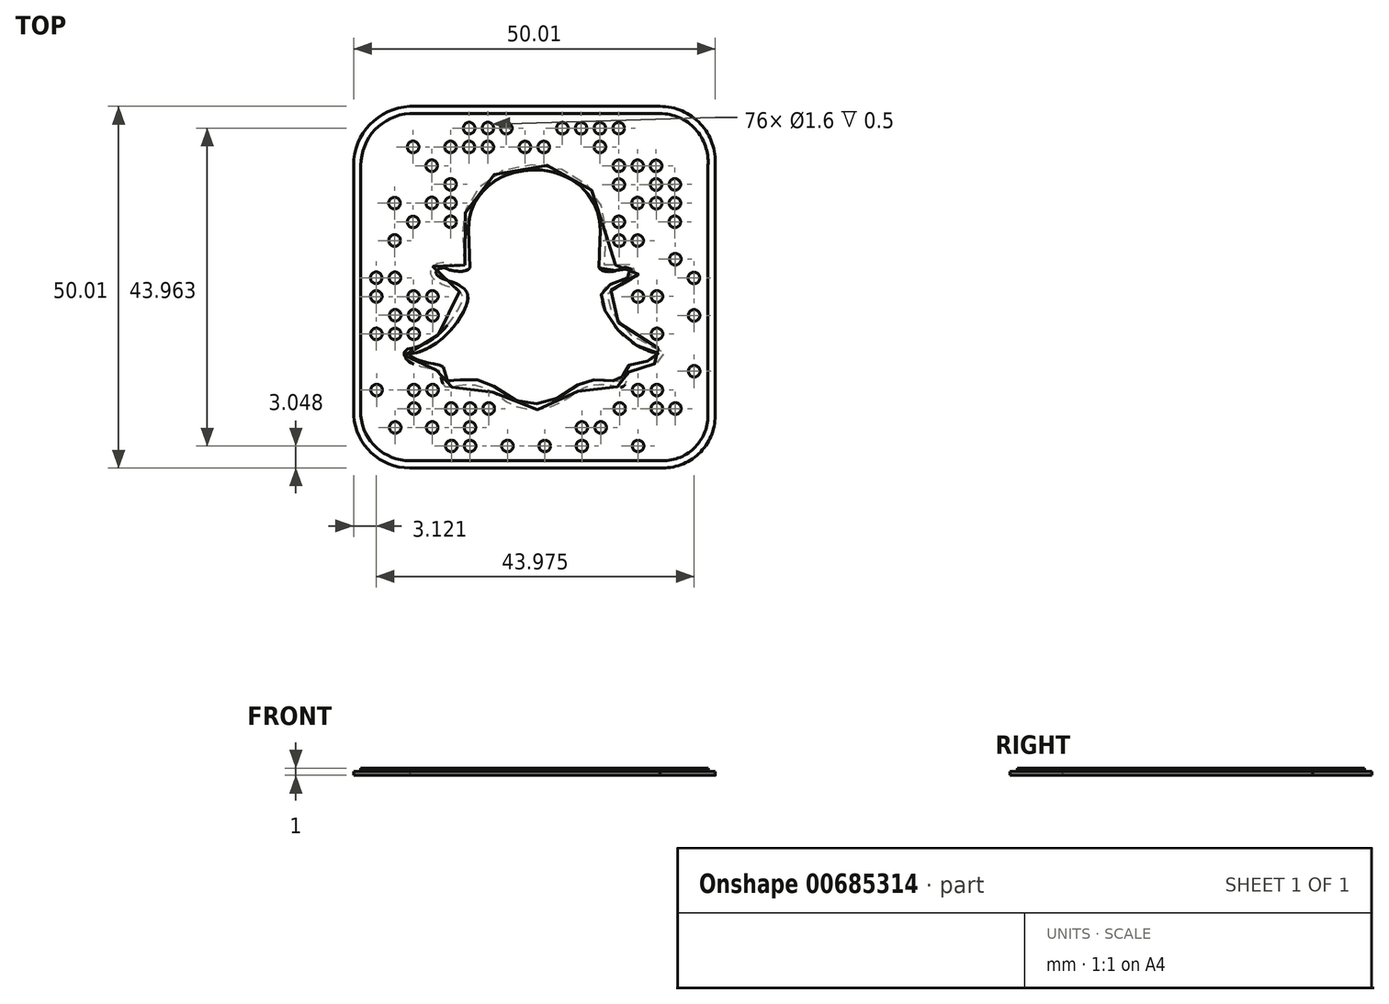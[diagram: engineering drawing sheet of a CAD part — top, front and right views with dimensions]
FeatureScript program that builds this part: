
annotation { "Feature Type Name" : "Feature", "Feature Type Description" : "" }
export const myFeature = defineFeature(function(context is Context, id is Id, definition is map)
    precondition{}
    {
        {
            var Q0;
            Q0=qCreatedBy(makeId("Top.planeOp"),FACE);
            var sketch = newSketch(context, id + "F0", { "sketchPlane" : qUnion([Q0])});
            skLineSegment(sketch, "E0", {"start": v(-18.15, 26.17) * mm, "end": v(16.46, 26.17) * mm});
            skLineSegment(sketch, "E1", {"start": v(-18.15, -23.83) * mm, "end": v(16.46, -23.83) * mm});
            skLineSegment(sketch, "E2", {"start": v(24.09, -16.6) * mm, "end": v(24.09, 18) * mm});
            skLineSegment(sketch, "E3", {"start": v(-25.91, -16.6) * mm, "end": v(-25.91, 18) * mm});
            skArc(sketch, "E4", {"start": v(-25.91, 18) * mm, "mid": v(-23.66, 23.64) * mm, "end": v(-18.15, 26.17) * mm});
            skArc(sketch, "E5", {"start": v(16.46, 26.17) * mm, "mid": v(22.05, 23.75) * mm, "end": v(24.09, 18) * mm});
            skArc(sketch, "E6", {"start": v(24.09, -16.6) * mm, "mid": v(21.83, -21.85) * mm, "end": v(16.46, -23.83) * mm});
            skArc(sketch, "E7", {"start": v(-18.15, -23.83) * mm, "mid": v(-23.45, -21.74) * mm, "end": v(-25.91, -16.6) * mm});
            skSolve(sketch);
        }
        {
            var Q0;
            Q0 = qSketchRegion(id + "F0", true);
            var Q1;
            Q1=makeQuery(id+"F0.imprint","IMPRINT",FACE,{"disambiguationData":[TD([[makeQuery(id+"F0.imprint","IMPRINT",EDGE,{"derivedFrom":sQuery(id+"F0.wireOp",EDGE,"E0")}),-1.0]])]});
            extrude(context, id + "F1", {"entities" : qUnion([Q0, Q1]), "depth" : 0.5 * mm, "offsetDistance" : 25 * mm});
        }
        {
            var Q0;
            Q0=makeQuery(id+"F1.opExtrude","CAP_FACE",FACE,{"disambiguationData":[OSD([sQuery(id+"F0.wireOp",EDGE,"E0"),sQuery(id+"F0.wireOp",EDGE,"E1"),sQuery(id+"F0.wireOp",EDGE,"E2"),sQuery(id+"F0.wireOp",EDGE,"E3"),sQuery(id+"F0.wireOp",EDGE,"E4"),sQuery(id+"F0.wireOp",EDGE,"E5"),sQuery(id+"F0.wireOp",EDGE,"E6"),sQuery(id+"F0.wireOp",EDGE,"E7")])],"isStart":false});
            var sketch = newSketch(context, id + "F2", { "sketchPlane" : qUnion([Q0])});
            skLineSegment(sketch, "E8", {"start": v(-18.15, 25.17) * mm, "end": v(16.46, 25.17) * mm});
            skLineSegment(sketch, "E9", {"start": v(23.09, 18) * mm, "end": v(23.09, -16.6) * mm});
            skLineSegment(sketch, "E10", {"start": v(16.46, -22.83) * mm, "end": v(-18.15, -22.83) * mm});
            skLineSegment(sketch, "E11", {"start": v(-24.91, -16.6) * mm, "end": v(-24.91, 18) * mm});
            skArc(sketch, "E12", {"start": v(-24.91, 18) * mm, "mid": v(-22.96, 22.94) * mm, "end": v(-18.15, 25.17) * mm});
            skArc(sketch, "E13", {"start": v(16.46, 25.17) * mm, "mid": v(21.34, 23.04) * mm, "end": v(23.09, 18) * mm});
            skArc(sketch, "E14", {"start": v(23.09, -16.6) * mm, "mid": v(21.12, -21.15) * mm, "end": v(16.46, -22.83) * mm});
            skArc(sketch, "E15", {"start": v(-18.15, -22.83) * mm, "mid": v(-22.74, -21.03) * mm, "end": v(-24.91, -16.6) * mm});
            skSolve(sketch);
        }
        {
            var Q0;
            Q0 = qSketchRegion(id + "F2", true);
            extrude(context, id + "F3", {"entities" : qUnion([Q0]), "operationType" : NewBodyOperationType.ADD, "depth" : 0.5 * mm, "offsetDistance" : 25 * mm});
        }
        {
            var Q0;
            Q0=makeQuery(id+"F1.opExtrude","CAP_FACE",FACE,{"disambiguationData":[OSD([sQuery(id+"F0.wireOp",EDGE,"E0"),sQuery(id+"F0.wireOp",EDGE,"E1"),sQuery(id+"F0.wireOp",EDGE,"E2"),sQuery(id+"F0.wireOp",EDGE,"E3"),sQuery(id+"F0.wireOp",EDGE,"E4"),sQuery(id+"F0.wireOp",EDGE,"E5"),sQuery(id+"F0.wireOp",EDGE,"E6"),sQuery(id+"F0.wireOp",EDGE,"E7")])],"isStart":false});
            var sketch = newSketch(context, id + "F4", { "sketchPlane" : qUnion([Q0])});
            skCircle(sketch, "E16", {"center": v(-2.22, 20.55) * mm, "radius": 0.8 * mm});
            skPoint(sketch, "E16.first.point", {"position": v(-2.2, 21.35) * mm});
            skPoint(sketch, "E16.second.point", {"position": v(-2.2, 19.75) * mm});
            skPoint(sketch, "E16.third.point", {"position": v(-1.7, 19.95) * mm});
            skCircle(sketch, "E17", {"center": v(0.39, 20.55) * mm, "radius": 0.8 * mm});
            skCircle(sketch, "E18", {"center": v(2.95, 23.15) * mm, "radius": 0.8 * mm});
            skCircle(sketch, "E19", {"center": v(5.55, 23.14) * mm, "radius": 0.8 * mm});
            skCircle(sketch, "E20", {"center": v(8.14, 23.15) * mm, "radius": 0.8 * mm});
            skCircle(sketch, "E21", {"center": v(10.75, 23.16) * mm, "radius": 0.8 * mm});
            skCircle(sketch, "E22", {"center": v(-4.79, 23.16) * mm, "radius": 0.8 * mm});
            skCircle(sketch, "E23", {"center": v(-7.34, 23.17) * mm, "radius": 0.8 * mm});
            skCircle(sketch, "E24", {"center": v(-9.94, 23.16) * mm, "radius": 0.8 * mm});
            skCircle(sketch, "E25", {"center": v(8.15, 20.58) * mm, "radius": 0.8 * mm});
            skCircle(sketch, "E26", {"center": v(-7.35, 20.58) * mm, "radius": 0.8 * mm});
            skCircle(sketch, "E27", {"center": v(-9.95, 20.56) * mm, "radius": 0.8 * mm});
            skCircle(sketch, "E28", {"center": v(-12.52, 20.57) * mm, "radius": 0.8 * mm});
            skCircle(sketch, "E29", {"center": v(-17.69, 20.57) * mm, "radius": 0.8 * mm});
            skCircle(sketch, "E30", {"center": v(-15.1, 17.97) * mm, "radius": 0.8 * mm});
            skCircle(sketch, "E31", {"center": v(10.78, 17.95) * mm, "radius": 0.8 * mm});
            skCircle(sketch, "E32", {"center": v(13.37, 17.95) * mm, "radius": 0.8 * mm});
            skCircle(sketch, "E33", {"center": v(15.92, 17.95) * mm, "radius": 0.8 * mm});
            skCircle(sketch, "E34", {"center": v(-12.5, 15.39) * mm, "radius": 0.8 * mm});
            skCircle(sketch, "E35", {"center": v(10.77, 15.36) * mm, "radius": 0.8 * mm});
            skCircle(sketch, "E36", {"center": v(15.91, 15.37) * mm, "radius": 0.8 * mm});
            skCircle(sketch, "E37", {"center": v(18.52, 15.38) * mm, "radius": 0.8 * mm});
            skCircle(sketch, "E38", {"center": v(18.52, 12.8) * mm, "radius": 0.8 * mm});
            skCircle(sketch, "E39", {"center": v(15.93, 12.79) * mm, "radius": 0.8 * mm});
            skCircle(sketch, "E40", {"center": v(13.34, 12.8) * mm, "radius": 0.8 * mm});
            skCircle(sketch, "E41", {"center": v(-12.52, 12.82) * mm, "radius": 0.8 * mm});
            skCircle(sketch, "E42", {"center": v(-15.1, 12.82) * mm, "radius": 0.8 * mm});
            skCircle(sketch, "E43", {"center": v(-20.26, 12.8) * mm, "radius": 0.8 * mm});
            skCircle(sketch, "E44", {"center": v(18.5, 10.22) * mm, "radius": 0.8 * mm});
            skCircle(sketch, "E45", {"center": v(10.77, 10.2) * mm, "radius": 0.8 * mm});
            skCircle(sketch, "E46", {"center": v(-12.5, 10.21) * mm, "radius": 0.8 * mm});
            skCircle(sketch, "E47", {"center": v(-17.68, 10.2) * mm, "radius": 0.8 * mm});
            skCircle(sketch, "E48", {"center": v(-20.24, 7.63) * mm, "radius": 0.8 * mm});
            skCircle(sketch, "E49", {"center": v(13.37, 7.62) * mm, "radius": 0.8 * mm});
            skCircle(sketch, "E50", {"center": v(10.81, 7.6) * mm, "radius": 0.8 * mm});
            skCircle(sketch, "E51", {"center": v(18.57, 5.04) * mm, "radius": 0.8 * mm});
            skCircle(sketch, "E52", {"center": v(-20.2, 2.46) * mm, "radius": 0.8 * mm});
            skCircle(sketch, "E53", {"center": v(-22.79, 2.47) * mm, "radius": 0.8 * mm});
            skCircle(sketch, "E54", {"center": v(21.15, 2.45) * mm, "radius": 0.8 * mm});
            skCircle(sketch, "E55", {"center": v(16.03, -0.12) * mm, "radius": 0.8 * mm});
            skCircle(sketch, "E56", {"center": v(13.42, -0.14) * mm, "radius": 0.8 * mm});
            skCircle(sketch, "E57", {"center": v(-15.02, -0.12) * mm, "radius": 0.8 * mm});
            skCircle(sketch, "E58", {"center": v(-17.6, -0.12) * mm, "radius": 0.8 * mm});
            skCircle(sketch, "E59", {"center": v(-22.78, -0.12) * mm, "radius": 0.8 * mm});
            skCircle(sketch, "E60", {"center": v(-20.16, -2.72) * mm, "radius": 0.8 * mm});
            skCircle(sketch, "E61", {"center": v(-17.56, -2.72) * mm, "radius": 0.8 * mm});
            skCircle(sketch, "E62", {"center": v(-14.98, -2.73) * mm, "radius": 0.8 * mm});
            skCircle(sketch, "E63", {"center": v(21.17, -2.73) * mm, "radius": 0.8 * mm});
            skCircle(sketch, "E64", {"center": v(16.04, -5.3) * mm, "radius": 0.8 * mm});
            skCircle(sketch, "E65", {"center": v(-17.58, -5.3) * mm, "radius": 0.8 * mm});
            skCircle(sketch, "E66", {"center": v(-20.17, -5.3) * mm, "radius": 0.8 * mm});
            skCircle(sketch, "E67", {"center": v(-22.75, -5.3) * mm, "radius": 0.8 * mm});
            skCircle(sketch, "E68", {"center": v(21.19, -10.46) * mm, "radius": 0.8 * mm});
            skCircle(sketch, "E69", {"center": v(16.02, -13.06) * mm, "radius": 0.8 * mm});
            skCircle(sketch, "E70", {"center": v(13.41, -13.06) * mm, "radius": 0.8 * mm});
            skCircle(sketch, "E71", {"center": v(-15, -13.06) * mm, "radius": 0.8 * mm});
            skCircle(sketch, "E72", {"center": v(-17.57, -13.06) * mm, "radius": 0.8 * mm});
            skCircle(sketch, "E73", {"center": v(-22.73, -13.06) * mm, "radius": 0.8 * mm});
            skCircle(sketch, "E74", {"center": v(-17.56, -15.61) * mm, "radius": 0.8 * mm});
            skCircle(sketch, "E75", {"center": v(-12.42, -15.61) * mm, "radius": 0.8 * mm});
            skCircle(sketch, "E76", {"center": v(-9.8, -15.61) * mm, "radius": 0.8 * mm});
            skCircle(sketch, "E77", {"center": v(-7.23, -15.61) * mm, "radius": 0.8 * mm});
            skCircle(sketch, "E78", {"center": v(10.87, -15.61) * mm, "radius": 0.8 * mm});
            skCircle(sketch, "E79", {"center": v(16.02, -15.61) * mm, "radius": 0.8 * mm});
            skCircle(sketch, "E80", {"center": v(18.59, -15.61) * mm, "radius": 0.8 * mm});
            skCircle(sketch, "E81", {"center": v(8.26, -18.23) * mm, "radius": 0.8 * mm});
            skCircle(sketch, "E82", {"center": v(5.65, -18.23) * mm, "radius": 0.8 * mm});
            skCircle(sketch, "E83", {"center": v(-9.82, -18.23) * mm, "radius": 0.8 * mm});
            skCircle(sketch, "E84", {"center": v(-15.04, -18.23) * mm, "radius": 0.8 * mm});
            skCircle(sketch, "E85", {"center": v(-20.16, -18.23) * mm, "radius": 0.8 * mm});
            skCircle(sketch, "E86", {"center": v(-12.4, -20.8) * mm, "radius": 0.8 * mm});
            skCircle(sketch, "E87", {"center": v(-9.82, -20.8) * mm, "radius": 0.8 * mm});
            skCircle(sketch, "E88", {"center": v(-4.65, -20.8) * mm, "radius": 0.8 * mm});
            skCircle(sketch, "E89", {"center": v(0.52, -20.8) * mm, "radius": 0.8 * mm});
            skCircle(sketch, "E90", {"center": v(5.66, -20.8) * mm, "radius": 0.8 * mm});
            skCircle(sketch, "E91", {"center": v(13.42, -20.8) * mm, "radius": 0.8 * mm});
            skSolve(sketch);
        }
        {
            var Q0;
            Q0 = qSketchRegion(id + "F4", true);
            extrude(context, id + "F5", {"entities" : qUnion([Q0]), "operationType" : NewBodyOperationType.REMOVE, "depth" : 0.5 * mm, "offsetDistance" : 25 * mm});
        }
        {
            var Q0;
            Q0=makeQuery(id+"F1.opExtrude","CAP_FACE",FACE,{"disambiguationData":[OSD([sQuery(id+"F0.wireOp",EDGE,"E0"),sQuery(id+"F0.wireOp",EDGE,"E1"),sQuery(id+"F0.wireOp",EDGE,"E2"),sQuery(id+"F0.wireOp",EDGE,"E3"),sQuery(id+"F0.wireOp",EDGE,"E4"),sQuery(id+"F0.wireOp",EDGE,"E5"),sQuery(id+"F0.wireOp",EDGE,"E6"),sQuery(id+"F0.wireOp",EDGE,"E7")])],"isStart":false});
            var sketch = newSketch(context, id + "F6", { "sketchPlane" : qUnion([Q0])});
            skLineSegment(sketch, "E92", {"start": v(-9.83, 3.85) * mm, "end": v(-10.03, 9.17) * mm});
            skFitSpline(sketch, "E93", {"points": [v(-10.03, 9.17) * mm, v(-9.61, 11.87) * mm, v(-7.7, 14.78) * mm, v(-4.63, 16.74) * mm, v(-1.42, 17.36) * mm, v(1.63, 17.1) * mm, v(5.33, 15.27) * mm, v(7.67, 12.03) * mm, v(8.18, 9.17) * mm, v(8, 3.85) * mm], "startDerivative": vector(1.47, 27.78) * mm, "endDerivative": vector(-2.36, -42.59) * mm});
            skFitSpline(sketch, "E94", {"points": [v(8, 3.85) * mm, v(8.53, 3.45) * mm, v(9.7, 3.32) * mm, v(10.86, 3.65) * mm, v(11.29, 3.85) * mm, v(11.97, 3.85) * mm, v(12.49, 3.6) * mm, v(12.66, 3.29) * mm, v(12.53, 2.9) * mm, v(12.11, 2.53) * mm, v(11.5, 2.24) * mm, v(10.58, 1.93) * mm, v(9.68, 1.58) * mm, v(8.97, 1.15) * mm, v(8.55, 0.69) * mm, v(8.33, 0.2) * mm, v(8.28, -0.48) * mm, v(8.48, -1.37) * mm, v(9.01, -2.42) * mm, v(9.61, -3.42) * mm, v(10.95, -5.05) * mm, v(12.39, -6.32) * mm, v(13.72, -7.15) * mm, v(15.57, -7.85) * mm, v(16.3, -8.03) * mm, v(16.34, -8.13) * mm, v(16.01, -8.5) * mm, v(14.99, -8.97) * mm, v(13.9, -9.3) * mm, v(12.7, -9.5) * mm, v(12.04, -9.64) * mm, v(11.8, -9.77) * mm, v(11.52, -10.13) * mm, v(11.34, -10.74) * mm, v(11.11, -11.8) * mm, v(11.06, -11.9) * mm, v(10.78, -11.9) * mm, v(9.96, -11.8) * mm, v(9.04, -11.65) * mm, v(7.92, -11.63) * mm, v(6.85, -11.7) * mm, v(5.97, -11.93) * mm, v(5.08, -12.36) * mm, v(3.22, -13.59) * mm, v(2.2, -14.25) * mm, v(0.92, -14.8) * mm, v(-0.64, -14.97) * mm, v(-1.37, -14.97) * mm, v(-2.95, -14.7) * mm, v(-5.02, -13.63) * mm, v(-6.5, -12.57) * mm, v(-7.57, -12.01) * mm, v(-8.4, -11.73) * mm, v(-9.35, -11.6) * mm, v(-10.1, -11.6) * mm, v(-11.01, -11.66) * mm, v(-12.06, -11.84) * mm, v(-12.71, -11.94) * mm, v(-12.86, -11.93) * mm, v(-12.97, -11.7) * mm, v(-13.08, -11.19) * mm, v(-13.18, -10.7) * mm, v(-13.44, -9.97) * mm, v(-13.8, -9.67) * mm, v(-14.71, -9.47) * mm, v(-15.73, -9.27) * mm, v(-16.51, -9.05) * mm, v(-17.35, -8.75) * mm, v(-17.8, -8.49) * mm, v(-18.09, -8.22) * mm, v(-18.14, -8.09) * mm, v(-17.7, -8) * mm, v(-16.41, -7.62) * mm, v(-14.86, -6.8) * mm, v(-13.68, -5.94) * mm, v(-12.19, -4.43) * mm, v(-10.84, -2.45) * mm, v(-10.25, -1.13) * mm, v(-10.1, -0.45) * mm, v(-10.13, 0) * mm, v(-10.2, 0.34) * mm, v(-10.51, 0.82) * mm, v(-11.2, 1.38) * mm], "startDerivative": vector(42.99, -41.33) * mm, "endDerivative": vector(-47.14, 26.01) * mm});
            skFitSpline(sketch, "E95", {"points": [v(-11.2, 1.38) * mm, v(-11.6, 1.63) * mm, v(-12.33, 1.89) * mm, v(-13.42, 2.26) * mm, v(-14.05, 2.6) * mm, v(-14.37, 2.87) * mm, v(-14.52, 3.12) * mm, v(-14.44, 3.45) * mm, v(-14.04, 3.74) * mm, v(-13.72, 3.82) * mm, v(-13.5, 3.85) * mm, v(-13.13, 3.76) * mm, v(-12.7, 3.58) * mm, v(-12.2, 3.44) * mm, v(-11.57, 3.38) * mm, v(-11.08, 3.35) * mm, v(-10.47, 3.46) * mm, v(-10.07, 3.63) * mm, v(-9.83, 3.85) * mm], "startDerivative": vector(-6.8, 4.63) * mm, "endDerivative": vector(4.73, 5.17) * mm});
            skSolve(sketch);
        }
        {
            var Q0;
            Q0 = qSketchRegion(id + "F6", true);
            extrude(context, id + "F7", {"entities" : qUnion([Q0]), "operationType" : NewBodyOperationType.REMOVE, "depth" : 20.5 * mm, "offsetDistance" : 25 * mm});
        }
        {
            var Q0;
            Q0=makeQuery(id+"F3.opExtrude","CAP_FACE",FACE,{"disambiguationData":[OSD([sQuery(id+"F2.wireOp",EDGE,"E8"),sQuery(id+"F2.wireOp",EDGE,"E9"),sQuery(id+"F2.wireOp",EDGE,"E10"),sQuery(id+"F2.wireOp",EDGE,"E11"),sQuery(id+"F2.wireOp",EDGE,"E12"),sQuery(id+"F2.wireOp",EDGE,"E13"),sQuery(id+"F2.wireOp",EDGE,"E14"),sQuery(id+"F2.wireOp",EDGE,"E15")])],"isStart":false});
            var sketch = newSketch(context, id + "F8", { "sketchPlane" : qUnion([Q0])});
            skLineSegment(sketch, "E96", {"start": v(-9.83, 3.85) * mm, "end": v(-10.03, 9.17) * mm});
            skFitSpline(sketch, "E97", {"points": [v(-10.03, 9.17) * mm, v(-9.62, 11.88) * mm, v(-7.7, 14.78) * mm, v(-4.64, 16.74) * mm, v(-1.42, 17.37) * mm, v(1.62, 17.1) * mm, v(5.33, 15.27) * mm, v(7.66, 12.03) * mm, v(8.17, 9.17) * mm, v(8, 3.85) * mm], "startDerivative": vector(1.47, 27.78) * mm, "endDerivative": vector(-2.36, -42.59) * mm});
            skFitSpline(sketch, "E98", {"points": [v(8, 3.85) * mm, v(8.53, 3.46) * mm, v(9.7, 3.32) * mm, v(10.85, 3.66) * mm, v(11.29, 3.85) * mm, v(11.96, 3.85) * mm, v(12.48, 3.6) * mm, v(12.66, 3.3) * mm, v(12.53, 2.9) * mm, v(12.1, 2.54) * mm, v(11.5, 2.24) * mm, v(10.58, 1.94) * mm, v(9.68, 1.59) * mm, v(8.97, 1.15) * mm, v(8.55, 0.7) * mm, v(8.32, 0.2) * mm, v(8.27, -0.47) * mm, v(8.48, -1.37) * mm, v(9, -2.42) * mm, v(9.6, -3.42) * mm, v(10.94, -5.04) * mm, v(12.38, -6.32) * mm, v(13.72, -7.14) * mm, v(15.57, -7.85) * mm, v(16.3, -8.02) * mm, v(16.34, -8.12) * mm, v(16, -8.5) * mm, v(14.98, -8.97) * mm, v(13.9, -9.3) * mm, v(12.7, -9.5) * mm, v(12.04, -9.64) * mm, v(11.8, -9.76) * mm, v(11.51, -10.13) * mm, v(11.34, -10.74) * mm, v(11.1, -11.8) * mm, v(11.06, -11.9) * mm, v(10.77, -11.9) * mm, v(9.95, -11.8) * mm, v(9.04, -11.64) * mm, v(7.92, -11.62) * mm, v(6.84, -11.7) * mm, v(5.97, -11.92) * mm, v(5.07, -12.36) * mm, v(3.22, -13.58) * mm, v(2.2, -14.24) * mm, v(0.92, -14.8) * mm, v(-0.64, -14.97) * mm, v(-1.37, -14.97) * mm, v(-2.95, -14.69) * mm, v(-5.02, -13.62) * mm, v(-6.5, -12.57) * mm, v(-7.58, -12) * mm, v(-8.4, -11.73) * mm, v(-9.36, -11.6) * mm, v(-10.1, -11.59) * mm, v(-11.02, -11.65) * mm, v(-12.06, -11.83) * mm, v(-12.71, -11.93) * mm, v(-12.86, -11.92) * mm, v(-12.98, -11.7) * mm, v(-13.09, -11.18) * mm, v(-13.18, -10.69) * mm, v(-13.44, -9.96) * mm, v(-13.8, -9.66) * mm, v(-14.72, -9.47) * mm, v(-15.73, -9.27) * mm, v(-16.52, -9.05) * mm, v(-17.35, -8.75) * mm, v(-17.8, -8.48) * mm, v(-18.1, -8.21) * mm, v(-18.14, -8.08) * mm, v(-17.71, -8) * mm, v(-16.42, -7.61) * mm, v(-14.86, -6.8) * mm, v(-13.68, -5.93) * mm, v(-12.2, -4.42) * mm, v(-10.84, -2.44) * mm, v(-10.25, -1.13) * mm, v(-10.1, -0.44) * mm, v(-10.13, 0) * mm, v(-10.2, 0.34) * mm, v(-10.51, 0.82) * mm, v(-11.2, 1.39) * mm], "startDerivative": vector(42.99, -41.33) * mm, "endDerivative": vector(-47.14, 26.01) * mm});
            skFitSpline(sketch, "E99", {"points": [v(-11.2, 1.39) * mm, v(-11.6, 1.63) * mm, v(-12.34, 1.9) * mm, v(-13.43, 2.27) * mm, v(-14.05, 2.6) * mm, v(-14.38, 2.87) * mm, v(-14.52, 3.13) * mm, v(-14.45, 3.46) * mm, v(-14.04, 3.75) * mm, v(-13.72, 3.83) * mm, v(-13.5, 3.85) * mm, v(-13.13, 3.76) * mm, v(-12.7, 3.59) * mm, v(-12.2, 3.45) * mm, v(-11.57, 3.39) * mm, v(-11.09, 3.36) * mm, v(-10.48, 3.46) * mm, v(-10.07, 3.64) * mm, v(-9.83, 3.85) * mm], "startDerivative": vector(-6.8, 4.63) * mm, "endDerivative": vector(4.73, 5.17) * mm});
            skFitSpline(sketch, "E100", {"points": [v(-10.55, 4.26) * mm, v(-10.71, 6.66) * mm, v(-10.76, 9.02) * mm, v(-10.62, 10.63) * mm, v(-10.41, 11.8) * mm, v(-9.87, 13.08) * mm, v(-8.87, 14.57) * mm, v(-7.54, 15.94) * mm, v(-5.8, 17.09) * mm, v(-4.02, 17.79) * mm, v(-1.8, 18.1) * mm, v(0.46, 18.1) * mm, v(2.56, 17.58) * mm, v(4.3, 16.88) * mm, v(5.99, 15.69) * mm, v(7.25, 14.26) * mm, v(8.09, 12.84) * mm, v(8.62, 11.65) * mm, v(8.9, 9.79) * mm, v(8.93, 8.01) * mm, v(8.74, 4.4) * mm, v(8.74, 4.23) * mm, v(8.8, 4.17) * mm, v(9.02, 4.09) * mm, v(9.5, 4.06) * mm, v(10.06, 4.15) * mm, v(10.56, 4.36) * mm, v(11.12, 4.53) * mm, v(11.9, 4.57) * mm, v(12.53, 4.4) * mm, v(13.15, 3.99) * mm, v(13.44, 3.45) * mm, v(13.41, 2.82) * mm, v(13.02, 2.27) * mm, v(12.47, 1.9) * mm, v(11.7, 1.54) * mm, v(10.84, 1.25) * mm, v(10.15, 0.99) * mm, v(9.51, 0.63) * mm, v(9.14, 0.23) * mm, v(9.02, -0.16) * mm, v(9.03, -0.66) * mm, v(9.35, -1.48) * mm, v(10.22, -3) * mm, v(11.76, -4.85) * mm, v(13.64, -6.29) * mm, v(15.04, -6.97) * mm, v(15.83, -7.2) * mm, v(16.46, -7.34) * mm, v(16.75, -7.46) * mm, v(16.9, -7.59) * mm, v(17.03, -7.8) * mm, v(17.08, -8.06) * mm, v(17.01, -8.43) * mm, v(16.7, -8.85) * mm, v(16.28, -9.17) * mm, v(15.58, -9.51) * mm, v(14.83, -9.77) * mm, v(14.1, -9.97) * mm, v(13.23, -10.17) * mm, v(12.65, -10.28) * mm, v(12.4, -10.3) * mm, v(12.27, -10.34) * mm, v(12.17, -10.46) * mm, v(12.11, -10.65) * mm, v(12, -11.18) * mm, v(11.9, -11.66) * mm, v(11.75, -12.1) * mm, v(11.62, -12.34) * mm, v(11.5, -12.48) * mm, v(11.31, -12.59) * mm, v(11.12, -12.64) * mm, v(10.79, -12.65) * mm, v(10.21, -12.57) * mm, v(8.96, -12.34) * mm, v(7.64, -12.34) * mm, v(6.69, -12.46) * mm, v(5.4, -13.03) * mm, v(4.23, -13.83) * mm, v(3.03, -14.66) * mm, v(1.66, -15.3) * mm, v(0.2, -15.72) * mm, v(-1.22, -15.74) * mm, v(-2.99, -15.54) * mm, v(-5.03, -14.54) * mm, v(-6.2, -13.7) * mm, v(-7.32, -13) * mm, v(-8.72, -12.5) * mm, v(-9.97, -12.34) * mm, v(-11.44, -12.48) * mm, v(-12.3, -12.68) * mm, v(-12.91, -12.7) * mm, v(-13.36, -12.48) * mm, v(-13.57, -12.18) * mm, v(-13.86, -11.15) * mm, v(-14, -10.62) * mm, v(-14.04, -10.45) * mm, v(-14.22, -10.34) * mm, v(-14.63, -10.27) * mm, v(-15.8, -10.05) * mm, v(-17.43, -9.54) * mm, v(-18.35, -9.04) * mm, v(-18.66, -8.72) * mm, v(-18.83, -8.36) * mm, v(-18.88, -8.11) * mm, v(-18.82, -7.77) * mm, v(-18.5, -7.44) * mm, v(-17.7, -7.25) * mm, v(-15.87, -6.5) * mm, v(-13.56, -4.78) * mm, v(-11.35, -1.71) * mm, v(-10.84, -0.46) * mm, v(-10.9, 0) * mm, v(-11.18, 0.45) * mm, v(-11.98, 0.96) * mm, v(-14.1, 1.74) * mm, v(-15.04, 2.55) * mm, v(-15.28, 3.23) * mm, v(-14.8, 4.17) * mm, v(-13.77, 4.62) * mm, v(-12.75, 4.47) * mm, v(-11.88, 4.13) * mm, v(-10.88, 4.06) * mm, v(-10.62, 4.14) * mm, v(-10.55, 4.26) * mm]});
            skSolve(sketch);
        }
        {
            var Q0;
            Q0 = qSketchRegion(id + "F8", true);
            extrude(context, id + "F9", {"entities" : qUnion([Q0]), "operationType" : NewBodyOperationType.REMOVE, "oppositeDirection" : true, "depth" : 0.3 * mm, "offsetDistance" : 25 * mm});
        }
    });
